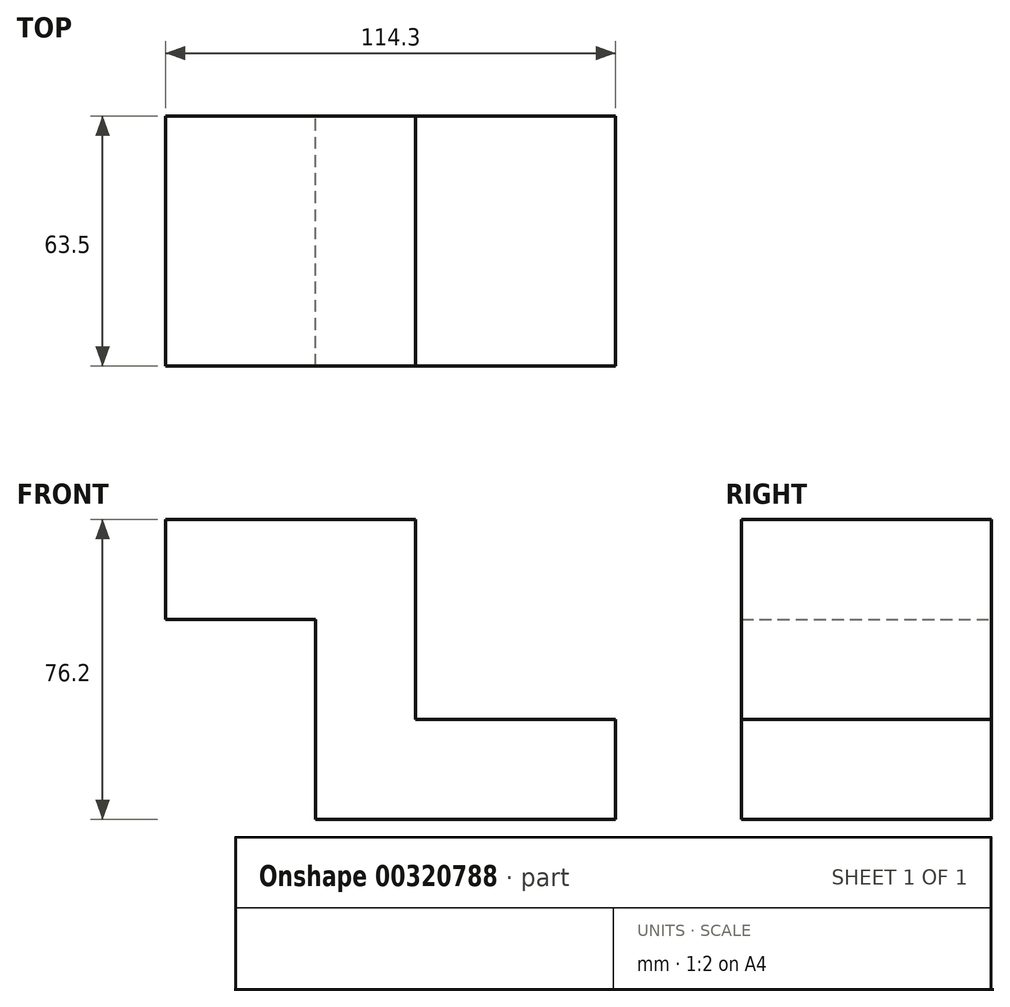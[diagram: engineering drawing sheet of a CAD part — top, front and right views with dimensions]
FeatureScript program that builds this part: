
annotation { "Feature Type Name" : "Feature", "Feature Type Description" : "" }
export const myFeature = defineFeature(function(context is Context, id is Id, definition is map)
    precondition{}
    {
        {
            var Q0;
            Q0=qCreatedBy(makeId("Front.planeOp"),FACE);
            var sketch = newSketch(context, id + "F0", { "sketchPlane" : qUnion([Q0])});
            skLineSegment(sketch, "E0", {"start": v(-39.83, 48.3) * mm, "end": v(-39.83, 22.9) * mm});
            skLineSegment(sketch, "E1", {"start": v(-39.83, 22.9) * mm, "end": v(-1.73, 22.9) * mm});
            skLineSegment(sketch, "E2", {"start": v(-1.73, 22.9) * mm, "end": v(-1.73, -27.9) * mm});
            skLineSegment(sketch, "E3", {"start": v(-1.73, -27.9) * mm, "end": v(74.47, -27.9) * mm});
            skLineSegment(sketch, "E4", {"start": v(74.47, -27.9) * mm, "end": v(74.47, -2.5) * mm});
            skLineSegment(sketch, "E5", {"start": v(74.47, -2.5) * mm, "end": v(23.67, -2.5) * mm});
            skLineSegment(sketch, "E6", {"start": v(23.67, -2.5) * mm, "end": v(23.67, 48.3) * mm});
            skLineSegment(sketch, "E7", {"start": v(23.67, 48.3) * mm, "end": v(-39.83, 48.3) * mm});
            skSolve(sketch);
        }
        {
            var Q0;
            Q0=makeQuery(id+"F0.imprint","IMPRINT",FACE,{"disambiguationData":[TD([[makeQuery(id+"F0.imprint","IMPRINT",EDGE,{"derivedFrom":sQuery(id+"F0.wireOp",EDGE,"E0")}),1.0]])]});
            extrude(context, id + "F1", {"entities" : qUnion([Q0]), "depth" : 63.5 * mm});
        }
    });
